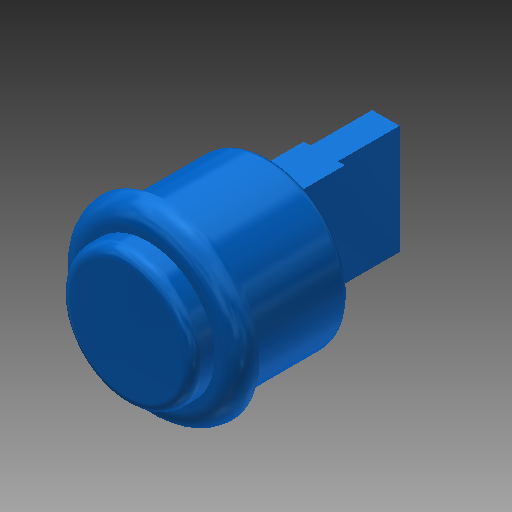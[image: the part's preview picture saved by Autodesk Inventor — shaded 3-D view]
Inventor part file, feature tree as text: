
AUTODESK INVENTOR PART (.ipt)
format: ipt  version: 2019 (Build 230136000, 136)  size: 210,944 bytes
history: native  units: in
note: dims shown in document units (in); Inventor stores cm internally (conversion verified against a paired STEP export)
features: extrude x5, sketch x5, fillet x3
ambient origin geometry x8: Origin, YZ Plane, XZ Plane, XY Plane, X Axis, Y Axis, Z Axis, Center Point
bodies: Solid1 (feature_tree)
feature tree (13):
  extrude  "Extrusion1"  Depth=0.5906in TaperAngle=0.0deg
  extrude  "Extrusion2"  Depth=0.1102in TaperAngle=0.0deg
  extrude  "Extrusion3"  Depth=0.126in TaperAngle=0.0deg
  fillet  "Fillet1"  Radius=0.0591in
  fillet  "Fillet2"  Radius=0.1161in
  fillet  "Fillet3"  Radius=0.0394in
  extrude  "Extrusion4"  Depth=0.6299in
  extrude  "Extrusion5"  Depth=0.1575in
  sketch  "Sketch1"  dims[d0=0.9252in d1=0.5906in d2=0.0in]
  sketch  "Sketch2"  dims[d3=1.063in d4=0.1102in d5=0.0in]
  sketch  "Sketch3"  dims[d8=0.7677in d9=0.126in d10=0.0in d11=0.0591in d12=0.1161in d13=0.0394in]
  sketch  "Sketch4"  dims[d14=0.2362in d16=0.6299in]
  sketch  "Sketch5"  dims[d17=0.315in d18=0.0in d19=0.1575in d21=0.6299in d22=0.3543in d23=0.0in]
